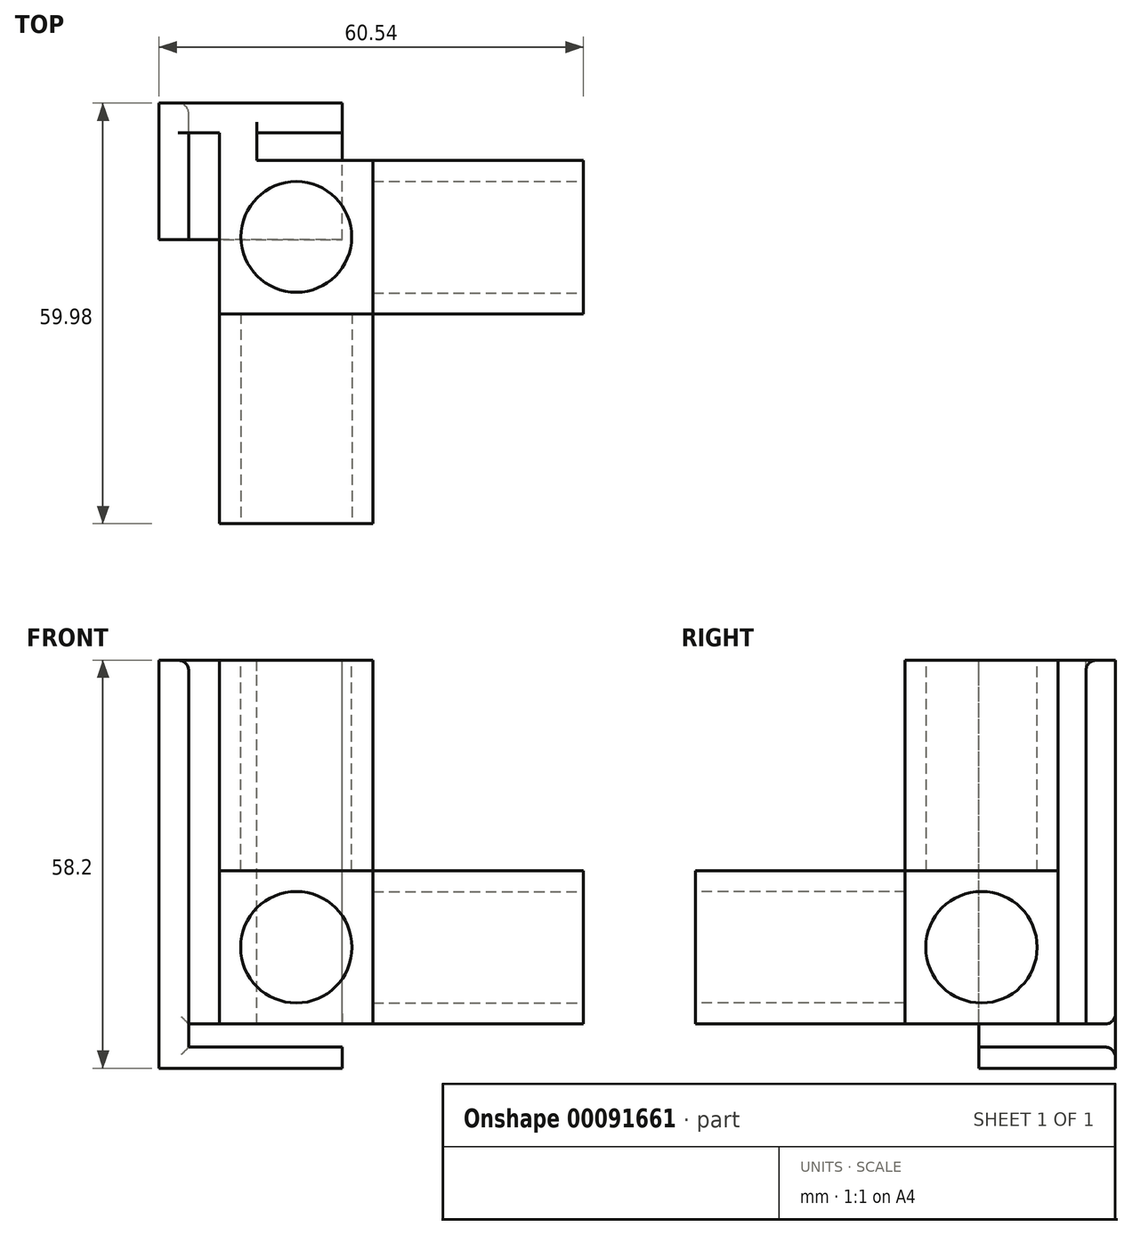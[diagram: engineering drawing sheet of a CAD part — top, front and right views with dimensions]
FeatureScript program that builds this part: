
annotation { "Feature Type Name" : "Feature", "Feature Type Description" : "" }
export const myFeature = defineFeature(function(context is Context, id is Id, definition is map)
    precondition{}
    {
        {
            var Q0;
            Q0=qCreatedBy(makeId("Front.planeOp"),FACE);
            var sketch = newSketch(context, id + "F0", { "sketchPlane" : qUnion([Q0])});
            skLineSegment(sketch, "E0.bottom", {"start": v(-42.3, 45.9) * mm, "end": v(-26.4, 45.9) * mm});
            skLineSegment(sketch, "E0.top", {"start": v(-42.3, 0) * mm, "end": v(-26.4, 0) * mm});
            skLineSegment(sketch, "E0.left", {"start": v(-42.3, 45.9) * mm, "end": v(-42.3, 0) * mm});
            skLineSegment(sketch, "E0.right", {"start": v(-26.4, 45.9) * mm, "end": v(-26.4, 15.9) * mm});
            skLineSegment(sketch, "E1.top", {"start": v(-42.3, 15.9) * mm, "end": v(-26.4, 15.9) * mm});
            skLineSegment(sketch, "E1.left", {"start": v(-42.3, 0) * mm, "end": v(-42.3, 15.9) * mm});
            skLineSegment(sketch, "E1.right", {"start": v(3.6, 0) * mm, "end": v(3.6, 15.9) * mm});
            skLineSegment(sketch, "E2", {"start": v(-26.4, 15.9) * mm, "end": v(-26.4, 0) * mm});
            skLineSegment(sketch, "E3", {"start": v(-26.4, 15.9) * mm, "end": v(3.6, 15.9) * mm});
            skLineSegment(sketch, "E4", {"start": v(-26.4, 0) * mm, "end": v(-26.4, 0) * mm});
            skLineSegment(sketch, "E5", {"start": v(-42.3, 15.9) * mm, "end": v(-42.3, 15.9) * mm});
            skLineSegment(sketch, "E6", {"start": v(-26.4, 0) * mm, "end": v(3.6, 0) * mm});
            skLineSegment(sketch, "E7.0", {"start": v(-45.3, 48.9) * mm, "end": v(-45.3, -3) * mm});
            skLineSegment(sketch, "E7.1", {"start": v(-45.3, -3) * mm, "end": v(-23.4, -3) * mm});
            skLineSegment(sketch, "E7.2", {"start": v(-23.4, 48.9) * mm, "end": v(-23.4, 18.9) * mm});
            skLineSegment(sketch, "E7.3", {"start": v(-23.4, 18.9) * mm, "end": v(6.6, 18.9) * mm});
            skLineSegment(sketch, "E7.4", {"start": v(6.6, -3) * mm, "end": v(6.6, 18.9) * mm});
            skLineSegment(sketch, "E7.5", {"start": v(-45.3, 48.9) * mm, "end": v(-23.4, 48.9) * mm});
            skLineSegment(sketch, "E7.6", {"start": v(-23.4, -3) * mm, "end": v(6.6, -3) * mm});
            skPoint(sketch, "E8", {"position": v(-34.36, 7.95) * mm});
            skPoint(sketch, "E8.positionSnap0", {"position": v(-26.4, 7.95) * mm});
            skPoint(sketch, "E8.positionSnap1", {"position": v(-34.36, 15.9) * mm});
            skCircle(sketch, "E9", {"center": v(-34.36, 7.95) * mm, "radius": 7.95 * mm});
            skLineSegment(sketch, "E10", {"start": v(-23.4, 18.9) * mm, "end": v(-45.3, 18.9) * mm});
            skLineSegment(sketch, "E11", {"start": v(-23.4, 18.9) * mm, "end": v(-23.4, -3) * mm});
            skSolve(sketch);
        }
        {
            var Q0;
            {var subQ1=sQuery(id+"F0.wireOp",EDGE,"E1.top");var subQ3=sQuery(id+"F0.wireOp",EDGE,"E9");var subQ4=makeQuery(id+"F0.imprint","INTERSECT",VERTEX,{"derivedFrom":[subQ1,subQ3]});Q0=makeQuery(id+"F0.imprint","IMPRINT",FACE,{"disambiguationData":[TD([[makeQuery(id+"F0.imprint","IMPRINT",EDGE,{"disambiguationData":[TD([[subQ4,-1.0]])],"derivedFrom":subQ3}),-1.0]])]});}
            var Q1;
            {var subQ0=sQuery(id+"F0.wireOp",EDGE,"E9");var subQ1=makeQuery(id+"F0.imprint","INTERSECT",VERTEX,{"derivedFrom":[sQuery(id+"F0.wireOp",EDGE,"E1.top"),subQ0]});Q1=makeQuery(id+"F0.imprint","IMPRINT",FACE,{"disambiguationData":[TD([[makeQuery(id+"F0.imprint","IMPRINT",EDGE,{"disambiguationData":[TD([[subQ1,1.0]])],"derivedFrom":subQ0}),1.0]])]});}
            var Q2;
            {var subQ5=sQuery(id+"F0.wireOp",EDGE,"E0.bottom");Q2=makeQuery(id+"F0.imprint","IMPRINT",FACE,{"disambiguationData":[TD([[makeQuery(id+"F0.imprint","IMPRINT",EDGE,{"derivedFrom":subQ5}),1.0]])]});}
            var Q3;
            {var subQ0=sQuery(id+"F0.wireOp",EDGE,"E1.right");Q3=makeQuery(id+"F0.imprint","IMPRINT",FACE,{"disambiguationData":[TD([[makeQuery(id+"F0.imprint","IMPRINT",EDGE,{"derivedFrom":subQ0}),1.0]])]});}
            var Q4;
            {var subQ0=sQuery(id+"F0.wireOp",EDGE,"E0.bottom");Q4=makeQuery(id+"F0.imprint","IMPRINT",FACE,{"disambiguationData":[TD([[makeQuery(id+"F0.imprint","IMPRINT",EDGE,{"derivedFrom":subQ0}),-1.0]])]});}
            var Q5;
            {var subQ0=sQuery(id+"F0.wireOp",EDGE,"E1.left");var subQ1=sQuery(id+"F0.wireOp",EDGE,"E0.top");var subQ2=makeQuery(id+"F0.imprint","INTERSECT",VERTEX,{"derivedFrom":[subQ1,subQ0]});Q5=makeQuery(id+"F0.imprint","IMPRINT",FACE,{"disambiguationData":[TD([[makeQuery(id+"F0.imprint","IMPRINT",EDGE,{"disambiguationData":[TD([[subQ2,-1.0]])],"derivedFrom":subQ1}),1.0]])]});}
            var Q6;
            {var subQ1=sQuery(id+"F0.wireOp",EDGE,"E0.top");var subQ3=sQuery(id+"F0.wireOp",EDGE,"E9");var subQ4=makeQuery(id+"F0.imprint","INTERSECT",VERTEX,{"derivedFrom":[subQ1,subQ3]});Q6=makeQuery(id+"F0.imprint","IMPRINT",FACE,{"disambiguationData":[TD([[makeQuery(id+"F0.imprint","IMPRINT",EDGE,{"disambiguationData":[TD([[subQ4,-1.0]])],"derivedFrom":subQ3}),-1.0]])]});}
            var Q7;
            {var subQ1=sQuery(id+"F0.wireOp",EDGE,"E1.top");var subQ3=sQuery(id+"F0.wireOp",EDGE,"E9");var subQ4=makeQuery(id+"F0.imprint","INTERSECT",VERTEX,{"derivedFrom":[subQ1,subQ3]});Q7=makeQuery(id+"F0.imprint","IMPRINT",FACE,{"disambiguationData":[TD([[makeQuery(id+"F0.imprint","IMPRINT",EDGE,{"disambiguationData":[TD([[subQ4,1.0]])],"derivedFrom":subQ3}),-1.0]])]});}
            var Q8;
            {var subQ5=sQuery(id+"F0.wireOp",EDGE,"E1.right");Q8=makeQuery(id+"F0.imprint","IMPRINT",FACE,{"disambiguationData":[TD([[makeQuery(id+"F0.imprint","IMPRINT",EDGE,{"derivedFrom":subQ5}),-1.0]])]});}
            var Q9;
            {var subQ4=sQuery(id+"F0.wireOp",EDGE,"E0.left");var subQ6=sQuery(id+"F0.wireOp",EDGE,"E10");var subQ8=makeQuery(id+"F0.imprint","INTERSECT",VERTEX,{"derivedFrom":[subQ4,subQ6]});Q9=makeQuery(id+"F0.imprint","IMPRINT",FACE,{"disambiguationData":[TD([[makeQuery(id+"F0.imprint","IMPRINT",EDGE,{"disambiguationData":[TD([[subQ8,1.0]])],"derivedFrom":subQ6}),1.0]])]});}
            var Q10;
            {var subQ3=sQuery(id+"F0.wireOp",EDGE,"E11");var subQ5=sQuery(id+"F0.wireOp",EDGE,"E3");var subQ8=makeQuery(id+"F0.imprint","INTERSECT",VERTEX,{"derivedFrom":[subQ5,subQ3]});Q10=makeQuery(id+"F0.imprint","IMPRINT",FACE,{"disambiguationData":[TD([[makeQuery(id+"F0.imprint","IMPRINT",EDGE,{"disambiguationData":[TD([[subQ8,-1.0]])],"derivedFrom":subQ3}),-1.0]])]});}
            var Q11;
            {var subQ14=sQuery(id+"F0.wireOp",EDGE,"E7.1");Q11=makeQuery(id+"F0.imprint","IMPRINT",FACE,{"disambiguationData":[TD([[makeQuery(id+"F0.imprint","IMPRINT",EDGE,{"derivedFrom":subQ14}),1.0]])]});}
            var Q12;
            {var subQ1=sQuery(id+"F0.wireOp",EDGE,"E0.right");var subQ3=sQuery(id+"F0.wireOp",EDGE,"E10");var subQ4=makeQuery(id+"F0.imprint","INTERSECT",VERTEX,{"derivedFrom":[subQ1,subQ3]});Q12=makeQuery(id+"F0.imprint","IMPRINT",FACE,{"disambiguationData":[TD([[makeQuery(id+"F0.imprint","IMPRINT",EDGE,{"disambiguationData":[TD([[subQ4,-1.0]])],"derivedFrom":subQ1}),1.0]])]});}
            extrude(context, id + "F1", {"entities" : qUnion([Q0, Q1, Q2, Q3, Q4, Q5, Q6, Q7, Q8, Q9, Q10, Q11, Q12]), "depth" : (15.9 + 6) * mm});
        }
        {
            var Q0;
            {var subQ14=sQuery(id+"F0.wireOp",EDGE,"E7.1");Q0=makeQuery(id+"F0.imprint","IMPRINT",FACE,{"disambiguationData":[TD([[makeQuery(id+"F0.imprint","IMPRINT",EDGE,{"derivedFrom":subQ14}),1.0]])]});}
            var Q1;
            {var subQ0=sQuery(id+"F0.wireOp",EDGE,"E9");var subQ1=makeQuery(id+"F0.imprint","INTERSECT",VERTEX,{"derivedFrom":[sQuery(id+"F0.wireOp",EDGE,"E1.top"),subQ0]});Q1=makeQuery(id+"F0.imprint","IMPRINT",FACE,{"disambiguationData":[TD([[makeQuery(id+"F0.imprint","IMPRINT",EDGE,{"disambiguationData":[TD([[subQ1,1.0]])],"derivedFrom":subQ0}),1.0]])]});}
            var Q2;
            {var subQ4=sQuery(id+"F0.wireOp",EDGE,"E0.left");var subQ6=sQuery(id+"F0.wireOp",EDGE,"E10");var subQ8=makeQuery(id+"F0.imprint","INTERSECT",VERTEX,{"derivedFrom":[subQ4,subQ6]});Q2=makeQuery(id+"F0.imprint","IMPRINT",FACE,{"disambiguationData":[TD([[makeQuery(id+"F0.imprint","IMPRINT",EDGE,{"disambiguationData":[TD([[subQ8,1.0]])],"derivedFrom":subQ6}),1.0]])]});}
            var Q3;
            {var subQ3=sQuery(id+"F0.wireOp",EDGE,"E11");var subQ5=sQuery(id+"F0.wireOp",EDGE,"E3");var subQ8=makeQuery(id+"F0.imprint","INTERSECT",VERTEX,{"derivedFrom":[subQ5,subQ3]});Q3=makeQuery(id+"F0.imprint","IMPRINT",FACE,{"disambiguationData":[TD([[makeQuery(id+"F0.imprint","IMPRINT",EDGE,{"disambiguationData":[TD([[subQ8,-1.0]])],"derivedFrom":subQ3}),-1.0]])]});}
            var Q4;
            {var subQ1=sQuery(id+"F0.wireOp",EDGE,"E0.right");var subQ3=sQuery(id+"F0.wireOp",EDGE,"E10");var subQ4=makeQuery(id+"F0.imprint","INTERSECT",VERTEX,{"derivedFrom":[subQ1,subQ3]});Q4=makeQuery(id+"F0.imprint","IMPRINT",FACE,{"disambiguationData":[TD([[makeQuery(id+"F0.imprint","IMPRINT",EDGE,{"disambiguationData":[TD([[subQ4,-1.0]])],"derivedFrom":subQ1}),1.0]])]});}
            var Q5;
            {var subQ1=sQuery(id+"F0.wireOp",EDGE,"E1.top");var subQ3=sQuery(id+"F0.wireOp",EDGE,"E9");var subQ4=makeQuery(id+"F0.imprint","INTERSECT",VERTEX,{"derivedFrom":[subQ1,subQ3]});Q5=makeQuery(id+"F0.imprint","IMPRINT",FACE,{"disambiguationData":[TD([[makeQuery(id+"F0.imprint","IMPRINT",EDGE,{"disambiguationData":[TD([[subQ4,1.0]])],"derivedFrom":subQ3}),-1.0]])]});}
            var Q6;
            {var subQ1=sQuery(id+"F0.wireOp",EDGE,"E1.top");var subQ3=sQuery(id+"F0.wireOp",EDGE,"E9");var subQ4=makeQuery(id+"F0.imprint","INTERSECT",VERTEX,{"derivedFrom":[subQ1,subQ3]});Q6=makeQuery(id+"F0.imprint","IMPRINT",FACE,{"disambiguationData":[TD([[makeQuery(id+"F0.imprint","IMPRINT",EDGE,{"disambiguationData":[TD([[subQ4,-1.0]])],"derivedFrom":subQ3}),-1.0]])]});}
            var Q7;
            {var subQ0=sQuery(id+"F0.wireOp",EDGE,"E1.left");var subQ1=sQuery(id+"F0.wireOp",EDGE,"E0.top");var subQ2=makeQuery(id+"F0.imprint","INTERSECT",VERTEX,{"derivedFrom":[subQ1,subQ0]});Q7=makeQuery(id+"F0.imprint","IMPRINT",FACE,{"disambiguationData":[TD([[makeQuery(id+"F0.imprint","IMPRINT",EDGE,{"disambiguationData":[TD([[subQ2,-1.0]])],"derivedFrom":subQ1}),1.0]])]});}
            var Q8;
            {var subQ1=sQuery(id+"F0.wireOp",EDGE,"E0.top");var subQ3=sQuery(id+"F0.wireOp",EDGE,"E9");var subQ4=makeQuery(id+"F0.imprint","INTERSECT",VERTEX,{"derivedFrom":[subQ1,subQ3]});Q8=makeQuery(id+"F0.imprint","IMPRINT",FACE,{"disambiguationData":[TD([[makeQuery(id+"F0.imprint","IMPRINT",EDGE,{"disambiguationData":[TD([[subQ4,-1.0]])],"derivedFrom":subQ3}),-1.0]])]});}
            extrude(context, id + "F2", {"entities" : qUnion([Q0, Q1, Q2, Q3, Q4, Q5, Q6, Q7, Q8]), "operationType" : NewBodyOperationType.ADD, "depth" : (15.8 + 6 + 30) * mm});
        }
        {
            var Q0;
            Q0=makeQuery(id+"F2.opExtrude","CAP_FACE",FACE,{"disambiguationData":[OSD([sQuery(id+"F0.wireOp",EDGE,"E7.0"),sQuery(id+"F0.wireOp",EDGE,"E7.1"),sQuery(id+"F0.wireOp",EDGE,"E10"),sQuery(id+"F0.wireOp",EDGE,"E11")])],"isStart":false});
            var sketch = newSketch(context, id + "F3", { "sketchPlane" : qUnion([Q0])});
            skCircle(sketch, "E12.0", {"center": v(-34.36, 7.95) * mm, "radius": 7.95 * mm});
            skSolve(sketch);
        }
        {
            var Q0;
            Q0=makeQuery(id+"F1.opExtrude","SWEPT_FACE",FACE,{"disambiguationData":[OSD([sQuery(id+"F0.wireOp",EDGE,"E7.5")])]});
            var sketch = newSketch(context, id + "F4", { "sketchPlane" : qUnion([Q0])});
            skPoint(sketch, "E13", {"position": v(-34.36, -3) * mm});
            skPoint(sketch, "E14", {"position": v(-26.4, -10.9) * mm});
            skPoint(sketch, "E15", {"position": v(-34.36, -10.9) * mm});
            skPoint(sketch, "E16", {"position": v(-62.98, 75) * mm});
            skPoint(sketch, "E17.orphan", {"position": v(-42.3, -3) * mm});
            skPoint(sketch, "E18.orphan", {"position": v(-26.4, -3) * mm});
            skPoint(sketch, "E19.orphan", {"position": v(-26.4, -18.8) * mm});
            skCircle(sketch, "E20", {"center": v(-34.36, -10.9) * mm, "radius": 7.9 * mm});
            skSolve(sketch);
        }
        {
            var Q0;
            Q0=makeQuery(id+"F1.opExtrude","SWEPT_FACE",FACE,{"disambiguationData":[OSD([sQuery(id+"F0.wireOp",EDGE,"E7.4")])]});
            var sketch = newSketch(context, id + "F5", { "sketchPlane" : qUnion([Q0])});
            skLineSegment(sketch, "E21.0", {"start": v(-18.9, 15.9) * mm, "end": v(-3, 15.9) * mm});
            skLineSegment(sketch, "E21.1", {"start": v(-18.9, 0) * mm, "end": v(-18.9, 15.9) * mm});
            skLineSegment(sketch, "E21.2", {"start": v(-18.9, 0) * mm, "end": v(-3, 0) * mm});
            skLineSegment(sketch, "E21.3", {"start": v(-3, 0) * mm, "end": v(-3, 15.9) * mm});
            skCircle(sketch, "E22", {"center": v(-10.95, 7.95) * mm, "radius": 7.95 * mm});
            skPoint(sketch, "E22.centerSnap0", {"position": v(-10.95, 0) * mm});
            skPoint(sketch, "E22.centerSnap1", {"position": v(-3, 7.95) * mm});
            skSolve(sketch);
        }
        {
            var Q0;
            Q0=makeQuery(id+"F3.imprint","IMPRINT",FACE,{"disambiguationData":[TD([[makeQuery(id+"F3.imprint","IMPRINT",EDGE,{"derivedFrom":sQuery(id+"F3.wireOp",EDGE,"E12.0")}),1.0]])]});
            extrude(context, id + "F6", {"entities" : qUnion([Q0]), "operationType" : NewBodyOperationType.REMOVE, "oppositeDirection" : true, "depth" : 30 * mm});
        }
        {
            var Q0;
            {var subQ0=sQuery(id+"F5.wireOp",EDGE,"E22");var subQ1=makeQuery(id+"F5.imprint","INTERSECT",VERTEX,{"derivedFrom":[sQuery(id+"F5.wireOp",EDGE,"E21.1"),subQ0]});Q0=makeQuery(id+"F5.imprint","IMPRINT",FACE,{"disambiguationData":[TD([[makeQuery(id+"F5.imprint","IMPRINT",EDGE,{"disambiguationData":[TD([[subQ1,1.0]])],"derivedFrom":subQ0}),1.0]])]});}
            extrude(context, id + "F7", {"entities" : qUnion([Q0]), "operationType" : NewBodyOperationType.REMOVE, "oppositeDirection" : true, "depth" : 30 * mm});
        }
        {
            var Q0;
            Q0=makeQuery(id+"F4.imprint","IMPRINT",FACE,{"disambiguationData":[TD([[makeQuery(id+"F4.imprint","IMPRINT",EDGE,{"derivedFrom":sQuery(id+"F4.wireOp",EDGE,"E20")}),1.0]])]});
            var Q1;
            Q1=sQuery(id+"F4.wireOp",EDGE,"E20");
            extrude(context, id + "F8", {"entities" : qUnion([Q0]), "operationType" : NewBodyOperationType.REMOVE, "surfaceEntities" : qUnion([Q1]), "oppositeDirection" : true, "depth" : 30 * mm});
        }
        {
            assignVariable(context, id + "F9", {"name" : "extrude", "anyValue" : 6 + 15.9 + 30});
        }
        {
            var Q0;
            Q0=makeQuery(id+"F1.opExtrude","SWEPT_FACE",FACE,{"disambiguationData":[OSD([sQuery(id+"F0.wireOp",EDGE,"E7.5")])]});
            var sketch = newSketch(context, id + "F10", { "sketchPlane" : qUnion([Q0])});
            skLineSegment(sketch, "E23", {"start": v(-45.3, 0) * mm, "end": v(-45.3, 8.18) * mm});
            skLineSegment(sketch, "E24", {"start": v(-45.3, 8.18) * mm, "end": v(-27.83, 8.18) * mm});
            skLineSegment(sketch, "E25", {"start": v(-27.83, 8.18) * mm, "end": v(-27.83, 3.95) * mm});
            skLineSegment(sketch, "E26", {"start": v(-27.83, 3.95) * mm, "end": v(-39.97, 3.95) * mm});
            skLineSegment(sketch, "E27", {"start": v(-39.97, 3.95) * mm, "end": v(-39.97, 0) * mm});
            skLineSegment(sketch, "E28", {"start": v(-45.3, 8.18) * mm, "end": v(-53.95, 8.18) * mm});
            skLineSegment(sketch, "E29", {"start": v(-53.95, 8.18) * mm, "end": v(-53.95, -11.32) * mm});
            skLineSegment(sketch, "E30", {"start": v(-53.95, -11.32) * mm, "end": v(-49.72, -11.32) * mm});
            skLineSegment(sketch, "E31", {"start": v(-49.72, -11.32) * mm, "end": v(-49.72, 3.95) * mm});
            skLineSegment(sketch, "E32", {"start": v(-49.72, 3.95) * mm, "end": v(-45.3, 3.95) * mm});
            skLineSegment(sketch, "E33", {"start": v(-49.72, 3.95) * mm, "end": v(-49.72, 8.18) * mm});
            skSolve(sketch);
        }
        {
            var Q0;
            {var subQ0=sQuery(id+"F10.wireOp",EDGE,"E29");Q0=makeQuery(id+"F10.imprint","IMPRINT",FACE,{"disambiguationData":[TD([[makeQuery(id+"F10.imprint","IMPRINT",EDGE,{"derivedFrom":subQ0}),1.0]])]});}
            var Q1;
            {var subQ3=sQuery(id+"F10.wireOp",EDGE,"E32");Q1=makeQuery(id+"F10.imprint","IMPRINT",FACE,{"disambiguationData":[TD([[makeQuery(id+"F10.imprint","IMPRINT",EDGE,{"derivedFrom":subQ3}),1.0]])]});}
            var Q2;
            {var subQ0=sQuery(id+"F10.wireOp",EDGE,"E24");Q2=makeQuery(id+"F10.imprint","IMPRINT",FACE,{"disambiguationData":[TD([[makeQuery(id+"F10.imprint","IMPRINT",EDGE,{"derivedFrom":subQ0}),-1.0]])]});}
            extrude(context, id + "F11", {"entities" : qUnion([Q0, Q1, Q2]), "operationType" : NewBodyOperationType.ADD, "oppositeDirection" : true, "depth" : (getVariable(context, 'extrude')) * mm});
        }
        {
            var Q0;
            {var subQ0=sQuery(id+"F0.wireOp",EDGE,"E7.1");Q0=makeQuery(id+"F11.boolean.opBoolean","MERGE",FACE,{"derivedFrom":[makeQuery(id+"F2.boolean.opBoolean","MERGE",FACE,{"derivedFrom":[makeQuery(id+"F1.opExtrude","SWEPT_FACE",FACE,{"disambiguationData":[OSD([subQ0,sQuery(id+"F0.wireOp",EDGE,"E7.6")])]}),makeQuery(id+"F2.opExtrude","SWEPT_FACE",FACE,{"disambiguationData":[OSD([subQ0])]})]}),makeQuery(id+"F11.opExtrude","CAP_FACE",FACE,{"disambiguationData":[OSD([sQuery(id+"F0.wireOp",EDGE,"E7.5"),sQuery(id+"F10.wireOp",EDGE,"E23"),sQuery(id+"F10.wireOp",EDGE,"E24"),sQuery(id+"F10.wireOp",EDGE,"E25"),sQuery(id+"F10.wireOp",EDGE,"E26"),sQuery(id+"F10.wireOp",EDGE,"E27"),sQuery(id+"F10.wireOp",EDGE,"E28"),sQuery(id+"F10.wireOp",EDGE,"E29"),sQuery(id+"F10.wireOp",EDGE,"E30"),sQuery(id+"F10.wireOp",EDGE,"E31"),sQuery(id+"F10.wireOp",EDGE,"E32")])],"isStart":false})]});}
            var sketch = newSketch(context, id + "F12", { "sketchPlane" : qUnion([Q0])});
            skLineSegment(sketch, "E34.0.0", {"start": v(6.6, 21.9) * mm, "end": v(-23.4, 21.9) * mm});
            skLineSegment(sketch, "E34.0.1", {"start": v(-23.4, 21.9) * mm, "end": v(-23.4, 51.8) * mm});
            skLineSegment(sketch, "E34.0.2", {"start": v(-23.4, 51.8) * mm, "end": v(-45.3, 51.8) * mm});
            skLineSegment(sketch, "E34.0.3", {"start": v(-45.3, 51.8) * mm, "end": v(-45.3, -3.95) * mm});
            skLineSegment(sketch, "E34.0.4", {"start": v(-45.3, -3.95) * mm, "end": v(-49.72, -3.95) * mm});
            skLineSegment(sketch, "E34.0.5", {"start": v(-49.72, -3.95) * mm, "end": v(-49.72, 11.32) * mm});
            skLineSegment(sketch, "E34.0.6", {"start": v(-49.72, 11.32) * mm, "end": v(-53.95, 11.32) * mm});
            skLineSegment(sketch, "E34.0.7", {"start": v(-53.95, 11.32) * mm, "end": v(-53.95, -8.18) * mm});
            skLineSegment(sketch, "E34.0.8", {"start": v(-53.95, -8.18) * mm, "end": v(-27.83, -8.18) * mm});
            skLineSegment(sketch, "E34.0.9", {"start": v(-27.83, -8.18) * mm, "end": v(-27.83, -3.95) * mm});
            skLineSegment(sketch, "E34.0.10", {"start": v(-27.83, -3.95) * mm, "end": v(-39.97, -3.95) * mm});
            skLineSegment(sketch, "E34.0.11", {"start": v(-39.97, -3.95) * mm, "end": v(-39.97, 0) * mm});
            skLineSegment(sketch, "E34.0.12", {"start": v(-39.97, 0) * mm, "end": v(6.6, 0) * mm});
            skLineSegment(sketch, "E34.0.13", {"start": v(6.6, 0) * mm, "end": v(6.6, 21.9) * mm});
            skLineSegment(sketch, "E35", {"start": v(-49.72, -3.95) * mm, "end": v(-49.72, -8.18) * mm});
            skSolve(sketch);
        }
        {
            var Q0;
            Q0=makeQuery(id+"F12.imprint","IMPRINT",FACE,{"disambiguationData":[TD([[makeQuery(id+"F12.imprint","IMPRINT",EDGE,{"derivedFrom":sQuery(id+"F12.wireOp",EDGE,"E34.0.5")}),-1.0]])]});
            extrude(context, id + "F13", {"entities" : qUnion([Q0]), "operationType" : NewBodyOperationType.ADD, "depth" : 6.3 * mm});
        }
        {
            var Q0;
            Q0=makeQuery(id+"F13.boolean.opBoolean","MERGE",FACE,{"derivedFrom":[makeQuery(id+"F11.opExtrude","SWEPT_FACE",FACE,{"disambiguationData":[OSD([sQuery(id+"F10.wireOp",EDGE,"E29")])]}),makeQuery(id+"F13.opExtrude","SWEPT_FACE",FACE,{"disambiguationData":[OSD([sQuery(id+"F12.wireOp",EDGE,"E34.0.7")])]})]});
            var sketch = newSketch(context, id + "F14", { "sketchPlane" : qUnion([Q0])});
            skLineSegment(sketch, "E36.0.0", {"start": v(11.32, 48.9) * mm, "end": v(-8.18, 48.9) * mm});
            skLineSegment(sketch, "E36.0.1", {"start": v(-8.18, 48.9) * mm, "end": v(-8.18, -9.3) * mm});
            skLineSegment(sketch, "E36.0.2", {"start": v(-8.18, -9.3) * mm, "end": v(11.32, -9.3) * mm});
            skLineSegment(sketch, "E36.0.3", {"start": v(11.32, -9.3) * mm, "end": v(11.32, 48.9) * mm});
            skLineSegment(sketch, "E37", {"start": v(-8.18, -6.3) * mm, "end": v(11.32, -6.3) * mm});
            skSolve(sketch);
        }
        {
            var Q0;
            {var subQ0=sQuery(id+"F14.wireOp",EDGE,"E36.0.2");Q0=makeQuery(id+"F14.imprint","IMPRINT",FACE,{"disambiguationData":[TD([[makeQuery(id+"F14.imprint","IMPRINT",EDGE,{"derivedFrom":subQ0}),1.0]])]});}
            var Q1;
            Q1=makeQuery(id+"F11.opExtrude","SWEPT_FACE",FACE,{"disambiguationData":[OSD([sQuery(id+"F10.wireOp",EDGE,"E25")])]});
            extrude(context, id + "F15", {"entities" : qUnion([Q0]), "operationType" : NewBodyOperationType.ADD, "endBound" : BoundingType.UP_TO_SURFACE, "oppositeDirection" : true, "endBoundEntityFace" : qUnion([Q1]), "depth" : 25 * mm});
        }
        {
            var Q0;
            Q0=makeQuery(id+"F15.opExtrude","SWEPT_EDGE",EDGE,{"disambiguationData":[OSD([sQuery(id+"F14.wireOp",EDGE,"E36.0.1"),sQuery(id+"F14.wireOp",EDGE,"E37")])]});
            var Q1;
            Q1=makeQuery(id+"F11.opExtrude","CAP_EDGE",EDGE,{"disambiguationData":[OSD([sQuery(id+"F10.wireOp",EDGE,"E24"),sQuery(id+"F10.wireOp",EDGE,"E28")])],"isStart":false});
            var Q2;
            Q2=makeQuery(id+"F11.opExtrude","CAP_EDGE",EDGE,{"disambiguationData":[OSD([sQuery(id+"F10.wireOp",EDGE,"E26")])],"isStart":true});
            var Q3;
            Q3=makeQuery(id+"F11.opExtrude","CAP_EDGE",EDGE,{"disambiguationData":[OSD([sQuery(id+"F10.wireOp",EDGE,"E31")])],"isStart":true});
            var Q4;
            Q4=makeQuery(id+"F13.opExtrude","SWEPT_EDGE",EDGE,{"disambiguationData":[OSD([sQuery(id+"F12.wireOp",EDGE,"E34.0.8"),sQuery(id+"F12.wireOp",EDGE,"E35")])]});
            fillet(context, id + "F16", {"entities" : qUnion([Q0, Q1, Q2, Q3, Q4]), "radius" : 1.5 * mm, "tangentPropagation" : true, "allowEdgeOverflow" : false});
        }
    });
